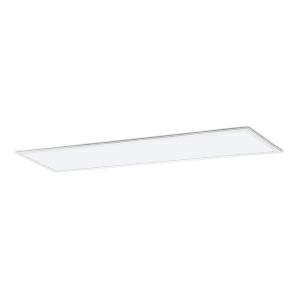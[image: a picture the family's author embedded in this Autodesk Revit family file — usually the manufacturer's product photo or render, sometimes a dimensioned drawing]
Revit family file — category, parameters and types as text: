
# Revit family: dotoo_fit_-_dfe_4000_840_d_ws_310x1245mm_00815304_6771
name_source: partatom
category: Lighting Fixtures
units: mm (PartAtom-declared; Revit-internal decimal feet)

## family parameters
Cut with Voids When Loaded = No
Host = Face
Light Source = No
Part Type = Normal
Room Calculation Point = No
Round Connector Dimension = Use Diameter
Shared = No

## types (1)
- DOTOO.fit - DFE 4000/840/D/WS/310x1245mm (1 x LED, 4300 lm, 4000K)
    Apparent Load = 30 VA
    Approval mark = CE
    CIE Flux Codes = 66 88 97 100 100
    Color Rendering = 80-89
    Color Temperature = 4000K
    Control Gear = Electronic ballast
    Default Elevation = 1800 mm
    Description = DFE 4000/840/D|Recessed modular luminaire|light source: LED Cold white   |work equipment: Power supply unit|luminous flux: 4300 lm|light distribution: Direct|direct ratio: approx. 100 %|color rendering index (CRI): >= 80|chromaticity tolerance:  3 SDCM|technology: Continuously dimmable|operation: External|luminaire body|material: Sectional aluminium|colour: White|weight (net): approx. 3.0 kg|mains lead: 0.80 m Connector 5 pin|design: Integrated version|glare control: Prism aperture|luminance(L65): <= 2800 cd/m|special features: DALI Load 1x, Direct light component with edge light and light-guide technology for homogenous light exit, Flicker-free, Strain relief with the possibility of through-wiring|
    Frequency = 50 Hz
    Height = 0 mm  [stored 0 ft]
    Lamp = 1 x LED
    Lamp Light Flux = 4300 lm
    Lamp count = 1
    Length = 1245 mm
    Luminous efficacy = 143 lm/W
    Manufacturer = Waldmann
    ModVariant = No
    Model = 00815304
    Mounting Place = Ceiling
    Mounting Type = Recessed
    Number of Poles = 1
    OnlyDefault = Yes
    Power Factor = 1
    Product Name = DOTOO.fit - DFE 4000/840/D/WS/310x1245mm
    Product group = Recessed luminaire
    ProductGroupID = 4
    Protection Class = Protection class II
    Protection Degree = IP 20
    RLX_Detail_Level = 1
    RLX_Emergency_Light_Flux = 0 lm
    RLX_Emergency_Type = 0
    RLX_Emergency_Type_DB = No
    RlxData = <blob elided: 18713 chars, md5=fa4b4cd0>
    Socket = socket
    Standby Power = 0 W
    System Light Flux = 4300 lm
    System Power = 30 W
    Type Comments = Product without accessories
    Type Image = dfe_dotoofit_1200x300.jpg
    URL = http://relux.com
    VarID = ---
    Voltage = 230 V
    Voltage Range = 220-240 V
    Weight = 0.00 kg
    Width = 310 mm

note: [stored X ft] marks values corroborated as IEEE doubles in the binary element streams (Revit-internal decimal feet)

## geometry (parser evidence)
native form markers: Blend x4, Sweep x11
no freeform markers — native parametric forms only
